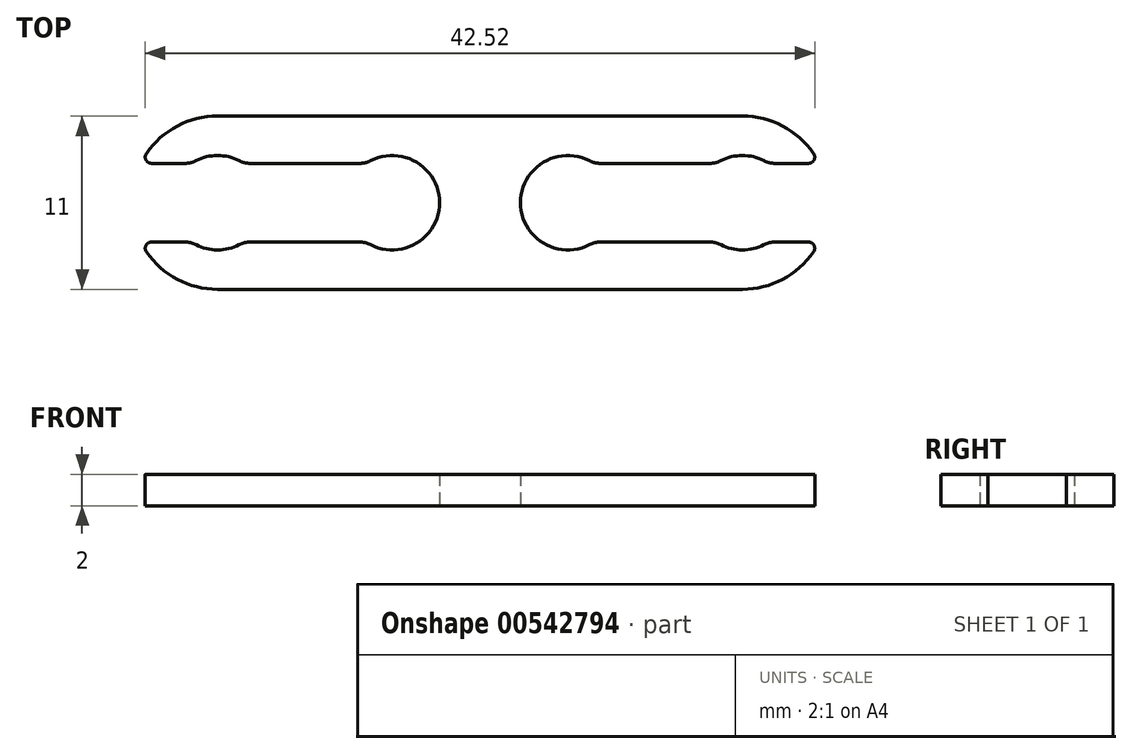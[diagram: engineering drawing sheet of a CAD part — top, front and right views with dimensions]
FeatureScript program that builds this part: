
annotation { "Feature Type Name" : "Feature", "Feature Type Description" : "" }
export const myFeature = defineFeature(function(context is Context, id is Id, definition is map)
    precondition{}
    {
        {
            var Q0;
            Q0=qCreatedBy(makeId("Top.planeOp"),FACE);
            var sketch = newSketch(context, id + "F0", { "sketchPlane" : qUnion([Q0])});
            skCircle(sketch, "E0", {"center": v(-5.57, 0) * mm, "radius": 3 * mm});
            skCircle(sketch, "E1", {"center": v(-16.67, 0) * mm, "radius": 3 * mm});
            skCircle(sketch, "E2", {"center": v(16.67, 0) * mm, "radius": 3 * mm});
            skCircle(sketch, "E3", {"center": v(5.57, 0) * mm, "radius": 3 * mm});
            skCircle(sketch, "E4", {"center": v(-16.67, 0) * mm, "radius": 5.5 * mm});
            skCircle(sketch, "E5", {"center": v(16.67, 0) * mm, "radius": 5.5 * mm});
            skLineSegment(sketch, "E6", {"start": v(-16.67, 5.5) * mm, "end": v(16.67, 5.5) * mm});
            skLineSegment(sketch, "E7", {"start": v(-16.67, -5.5) * mm, "end": v(16.67, -5.5) * mm});
            skLineSegment(sketch, "E8.bottom", {"start": v(-26.17, 2.5) * mm, "end": v(-7.17, 2.5) * mm});
            skLineSegment(sketch, "E8.top", {"start": v(-26.17, -2.5) * mm, "end": v(-7.17, -2.5) * mm});
            skLineSegment(sketch, "E8.left", {"start": v(-26.17, 2.5) * mm, "end": v(-26.17, -2.5) * mm});
            skLineSegment(sketch, "E8.right", {"start": v(-7.17, 2.5) * mm, "end": v(-7.17, -2.5) * mm});
            skLineSegment(sketch, "E9.bottom", {"start": v(26.17, 2.5) * mm, "end": v(7.17, 2.5) * mm});
            skLineSegment(sketch, "E9.top", {"start": v(26.17, -2.5) * mm, "end": v(7.17, -2.5) * mm});
            skLineSegment(sketch, "E9.left", {"start": v(26.17, 2.5) * mm, "end": v(26.17, -2.5) * mm});
            skLineSegment(sketch, "E9.right", {"start": v(7.17, 2.5) * mm, "end": v(7.17, -2.5) * mm});
            skSolve(sketch);
        }
        {
            var Q0;
            {var subQ2=sQuery(id+"F0.wireOp",EDGE,"E8.bottom");var subQ4=sQuery(id+"F0.wireOp",EDGE,"E1");var subQ5=makeQuery(id+"F0.imprint","INTERSECT",VERTEX,{"disambiguationData":[OD(0.0)],"derivedFrom":[subQ4,subQ2]});Q0=makeQuery(id+"F0.imprint","IMPRINT",FACE,{"disambiguationData":[TD([[makeQuery(id+"F0.imprint","IMPRINT",EDGE,{"disambiguationData":[TD([[subQ5,1.0]])],"derivedFrom":subQ4}),-1.0]])]});}
            var Q1;
            {var subQ0=sQuery(id+"F0.wireOp",EDGE,"E8.top");var subQ3=sQuery(id+"F0.wireOp",EDGE,"E1");var subQ4=makeQuery(id+"F0.imprint","INTERSECT",VERTEX,{"disambiguationData":[OD(0.0)],"derivedFrom":[subQ3,subQ0]});Q1=makeQuery(id+"F0.imprint","IMPRINT",FACE,{"disambiguationData":[TD([[makeQuery(id+"F0.imprint","IMPRINT",EDGE,{"disambiguationData":[TD([[subQ4,-1.0]])],"derivedFrom":subQ3}),-1.0]])]});}
            var Q2;
            {var subQ2=sQuery(id+"F0.wireOp",EDGE,"E9.bottom");var subQ5=sQuery(id+"F0.wireOp",EDGE,"E2");var subQ7=makeQuery(id+"F0.imprint","INTERSECT",VERTEX,{"disambiguationData":[OD(0.0)],"derivedFrom":[subQ5,subQ2]});Q2=makeQuery(id+"F0.imprint","IMPRINT",FACE,{"disambiguationData":[TD([[makeQuery(id+"F0.imprint","IMPRINT",EDGE,{"disambiguationData":[TD([[subQ7,1.0]])],"derivedFrom":subQ5}),-1.0]])]});}
            var Q3;
            {var subQ0=sQuery(id+"F0.wireOp",EDGE,"E9.top");var subQ3=sQuery(id+"F0.wireOp",EDGE,"E2");var subQ7=makeQuery(id+"F0.imprint","INTERSECT",VERTEX,{"disambiguationData":[OD(0.0)],"derivedFrom":[subQ3,subQ0]});Q3=makeQuery(id+"F0.imprint","IMPRINT",FACE,{"disambiguationData":[TD([[makeQuery(id+"F0.imprint","IMPRINT",EDGE,{"disambiguationData":[TD([[subQ7,-1.0]])],"derivedFrom":subQ3}),-1.0]])]});}
            var Q4;
            {var subQ6=sQuery(id+"F0.wireOp",EDGE,"E6");Q4=makeQuery(id+"F0.imprint","IMPRINT",FACE,{"disambiguationData":[TD([[makeQuery(id+"F0.imprint","IMPRINT",EDGE,{"derivedFrom":subQ6}),-1.0]])]});}
            extrude(context, id + "F1", {"entities" : qUnion([Q0, Q1, Q2, Q3, Q4]), "depth" : 2 * mm, "offsetDistance" : 25 * mm});
        }
        {
            var Q0;
            {var subQ0=sQuery(id+"F0.wireOp",EDGE,"E8.bottom");var subQ1=sQuery(id+"F0.wireOp",EDGE,"E1");Q0=makeQuery(id+"F1.opExtrude","SWEPT_EDGE",EDGE,{"disambiguationData":[OSD([subQ1,subQ0]),TDD([makeQuery(id+"F0.imprint","INTERSECT",VERTEX,{"disambiguationData":[OD(0.0)],"derivedFrom":[subQ1,subQ0]})])]});}
            var Q1;
            {var subQ0=sQuery(id+"F0.wireOp",EDGE,"E8.bottom");var subQ1=sQuery(id+"F0.wireOp",EDGE,"E1");Q1=makeQuery(id+"F1.opExtrude","SWEPT_EDGE",EDGE,{"disambiguationData":[OSD([subQ1,subQ0]),TDD([makeQuery(id+"F0.imprint","INTERSECT",VERTEX,{"disambiguationData":[OD(1.0)],"derivedFrom":[subQ1,subQ0]})])]});}
            var Q2;
            Q2=makeQuery(id+"F1.opExtrude","SWEPT_EDGE",EDGE,{"disambiguationData":[OSD([sQuery(id+"F0.wireOp",EDGE,"E0"),sQuery(id+"F0.wireOp",EDGE,"E8.bottom")])]});
            var Q3;
            {var subQ0=sQuery(id+"F0.wireOp",EDGE,"E8.top");var subQ1=sQuery(id+"F0.wireOp",EDGE,"E1");Q3=makeQuery(id+"F1.opExtrude","SWEPT_EDGE",EDGE,{"disambiguationData":[OSD([subQ1,subQ0]),TDD([makeQuery(id+"F0.imprint","INTERSECT",VERTEX,{"disambiguationData":[OD(0.0)],"derivedFrom":[subQ1,subQ0]})])]});}
            var Q4;
            {var subQ0=sQuery(id+"F0.wireOp",EDGE,"E8.top");var subQ1=sQuery(id+"F0.wireOp",EDGE,"E1");Q4=makeQuery(id+"F1.opExtrude","SWEPT_EDGE",EDGE,{"disambiguationData":[OSD([subQ1,subQ0]),TDD([makeQuery(id+"F0.imprint","INTERSECT",VERTEX,{"disambiguationData":[OD(1.0)],"derivedFrom":[subQ1,subQ0]})])]});}
            var Q5;
            Q5=makeQuery(id+"F1.opExtrude","SWEPT_EDGE",EDGE,{"disambiguationData":[OSD([sQuery(id+"F0.wireOp",EDGE,"E0"),sQuery(id+"F0.wireOp",EDGE,"E8.top")])]});
            var Q6;
            Q6=makeQuery(id+"F1.opExtrude","SWEPT_EDGE",EDGE,{"disambiguationData":[OSD([sQuery(id+"F0.wireOp",EDGE,"E3"),sQuery(id+"F0.wireOp",EDGE,"E9.bottom")])]});
            var Q7;
            {var subQ0=sQuery(id+"F0.wireOp",EDGE,"E9.bottom");var subQ1=sQuery(id+"F0.wireOp",EDGE,"E2");Q7=makeQuery(id+"F1.opExtrude","SWEPT_EDGE",EDGE,{"disambiguationData":[OSD([subQ1,subQ0]),TDD([makeQuery(id+"F0.imprint","INTERSECT",VERTEX,{"disambiguationData":[OD(0.0)],"derivedFrom":[subQ1,subQ0]})])]});}
            var Q8;
            {var subQ0=sQuery(id+"F0.wireOp",EDGE,"E9.bottom");var subQ1=sQuery(id+"F0.wireOp",EDGE,"E2");Q8=makeQuery(id+"F1.opExtrude","SWEPT_EDGE",EDGE,{"disambiguationData":[OSD([subQ1,subQ0]),TDD([makeQuery(id+"F0.imprint","INTERSECT",VERTEX,{"disambiguationData":[OD(1.0)],"derivedFrom":[subQ1,subQ0]})])]});}
            var Q9;
            Q9=makeQuery(id+"F1.opExtrude","SWEPT_EDGE",EDGE,{"disambiguationData":[OSD([sQuery(id+"F0.wireOp",EDGE,"E3"),sQuery(id+"F0.wireOp",EDGE,"E9.top")])]});
            var Q10;
            {var subQ0=sQuery(id+"F0.wireOp",EDGE,"E9.top");var subQ1=sQuery(id+"F0.wireOp",EDGE,"E2");Q10=makeQuery(id+"F1.opExtrude","SWEPT_EDGE",EDGE,{"disambiguationData":[OSD([subQ1,subQ0]),TDD([makeQuery(id+"F0.imprint","INTERSECT",VERTEX,{"disambiguationData":[OD(0.0)],"derivedFrom":[subQ1,subQ0]})])]});}
            var Q11;
            {var subQ0=sQuery(id+"F0.wireOp",EDGE,"E9.top");var subQ1=sQuery(id+"F0.wireOp",EDGE,"E2");Q11=makeQuery(id+"F1.opExtrude","SWEPT_EDGE",EDGE,{"disambiguationData":[OSD([subQ1,subQ0]),TDD([makeQuery(id+"F0.imprint","INTERSECT",VERTEX,{"disambiguationData":[OD(1.0)],"derivedFrom":[subQ1,subQ0]})])]});}
            fillet(context, id + "F2", {"entities" : qUnion([Q0, Q1, Q2, Q3, Q4, Q5, Q6, Q7, Q8, Q9, Q10, Q11]), "radius" : 1.5 * mm, "tangentPropagation" : true, "allowEdgeOverflow" : false});
        }
        {
            var Q0;
            Q0=makeQuery(id+"F1.opExtrude","SWEPT_EDGE",EDGE,{"disambiguationData":[OSD([sQuery(id+"F0.wireOp",EDGE,"E5"),sQuery(id+"F0.wireOp",EDGE,"E9.bottom")])]});
            var Q1;
            Q1=makeQuery(id+"F1.opExtrude","SWEPT_EDGE",EDGE,{"disambiguationData":[OSD([sQuery(id+"F0.wireOp",EDGE,"E5"),sQuery(id+"F0.wireOp",EDGE,"E9.top")])]});
            var Q2;
            Q2=makeQuery(id+"F1.opExtrude","SWEPT_EDGE",EDGE,{"disambiguationData":[OSD([sQuery(id+"F0.wireOp",EDGE,"E4"),sQuery(id+"F0.wireOp",EDGE,"E8.bottom")])]});
            var Q3;
            Q3=makeQuery(id+"F1.opExtrude","SWEPT_EDGE",EDGE,{"disambiguationData":[OSD([sQuery(id+"F0.wireOp",EDGE,"E4"),sQuery(id+"F0.wireOp",EDGE,"E8.top")])]});
            fillet(context, id + "F3", {"entities" : qUnion([Q0, Q1, Q2, Q3]), "radius" : .4 * mm, "tangentPropagation" : true, "allowEdgeOverflow" : false});
        }
    });
